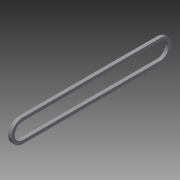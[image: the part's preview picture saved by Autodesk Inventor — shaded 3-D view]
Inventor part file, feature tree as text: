
AUTODESK INVENTOR PART (.ipt)
format: ipt  version: 2015 SP1 (Build 190203100, 203)  size: 86,528 bytes
history: native  units: in
note: dims shown in document units (in); Inventor stores cm internally (conversion verified against a paired STEP export)
features: extrude x1, sketch x1
ambient origin geometry x8: Origin, YZ Plane, XZ Plane, XY Plane, X Axis, Y Axis, Z Axis, Center Point
bodies: Solid1 (feature_tree)
feature tree (2):
  extrude  "Extrusion1"  Depth=0.625in
  sketch  "Sketch1"  dims[d0=10.5in d3=0.625in d4=0.625in d5=0.625in d6=0.0in d7=0.625in d8=180.0deg d9=0.625in d10=0.625in d11=0.25in d12=0.25in d13=0.0in]
